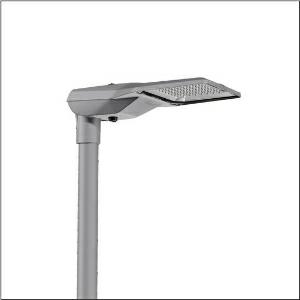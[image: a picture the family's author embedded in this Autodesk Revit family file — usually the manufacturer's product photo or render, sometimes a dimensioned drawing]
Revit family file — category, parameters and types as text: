
# Revit family: streetlight_sl_21_midi___st0_5a_5xe3b43t08mb_3943
name_source: partatom
category: Lighting Fixtures
units: mm (PartAtom-declared; Revit-internal decimal feet)

## family parameters
Cut with Voids When Loaded = No
Host = Face
Light Source = No
Part Type = Normal
Room Calculation Point = No
Round Connector Dimension = Use Diameter
Shared = No

## types (1)
- --- (1 x LED, 20180 lm, 147 W, 4000K)
    Apparent Load = 147 VA
    CIE Flux Codes = 41 75 97 100 100
    Color Rendering = 70
    Color Temperature = 4000K
    Default Elevation = 1800 mm
    Description = Streetlight SL 21 midi, mast luminaire, primary light control with lens, of PMMA, primary optical cover: cover, of toughened safety glass, transparent, light distribution: ST0.5a, light emission: direct distribution, primary light characteristic: asymmetric, installation type: side-entry, post-top, LED, High Power LED, rated luminous flux: 20.180lm, luminous efficacy: 137lm/W, light colour: 740, colour temperature: 4000K, control gear: D4i, control: overheat protection, constant luminous flux control, time-dependent luminous flux control, flexible luminous flux parameterisation, pre-setting: logarithmic dimming characteristic, mains connection: 230..240V, AC, 50/60Hz, start of lifetime: 147W, end of service life: 155W, reduction: 65W, luminaire housing, of diecast aluminium, powder-coated, SITECO metallic grey (DB 702S), corrosivity category C5 high according to DIN EN ISO 12944, please order mast flange separately, inclination adjustable: 0°, 5°, 10°, 15°, sealing non-destructively replaceable, multi-level sealing system, length: 644mm, width: 335mm, height: 110mm, mast flange for spigot size: 42mm (side-entry): 5XC10008XM4, 60/48mm (side-entry/post-top): 5XC10108XM2, 76/60mm (side-entry/post-top): 5XC10108XM1, mounting height: 4..8m, Smart Interface below and above, protection rating (complete): IP66, insulation class (complete): insulation class II (safety insulation), certification: CE, ENEC, ENEC+, VDE, impact resistance: IK10, permissible operating ambient temperature for outdoor applications: -40..+50°C, standard-compliant lighting for roads and squares, packaging unit: 1 piece

Light Distribution: ST0.5a
    Height = 111 mm
    Lamp = 1 x LED
    Lamp Light Flux = 20180 lm
    Lamp Power = 147 W
    Lamp count = 1
    Length = 644 mm
    Luminous efficacy = 137 lm/W
    Manufacturer = Siteco
    ModVariant = No
    Model = 5XE3B43T08MB
    Number of Poles = 1
    OnlyDefault = Yes
    Power Factor = 1
    Product Name = Streetlight SL 21 midi | ST0.5a
    Product group = mast luminaire | pylon top
    ProductGroupID = 6100
    Protection Class = Protection class II
    Protection Degree = IP 66
    RLX_Detail_Level = 1
    RLX_Emergency_Light_Flux = 0 lm
    RLX_Emergency_Type = 0
    RLX_Emergency_Type_DB = No
    RlxData = <blob elided: 38145 chars, md5=40ec39c1>
    Socket = socket
    Standby Power = 0 W
    System Light Flux = 20180 lm
    System Power = 147 W
    Type Comments = factory setting: luminous flux: 100 % | dim-lin: 254 | 750 mA
    Type Image = l_1004304.jpg
    URL = http://relux.com
    VarID = @adj_189071
    Voltage = 0 V
    Weight = 0.00 kg
    Width = 336 mm

## geometry (parser evidence)
native form markers: Blend x4, Sweep x10
no freeform markers — native parametric forms only
